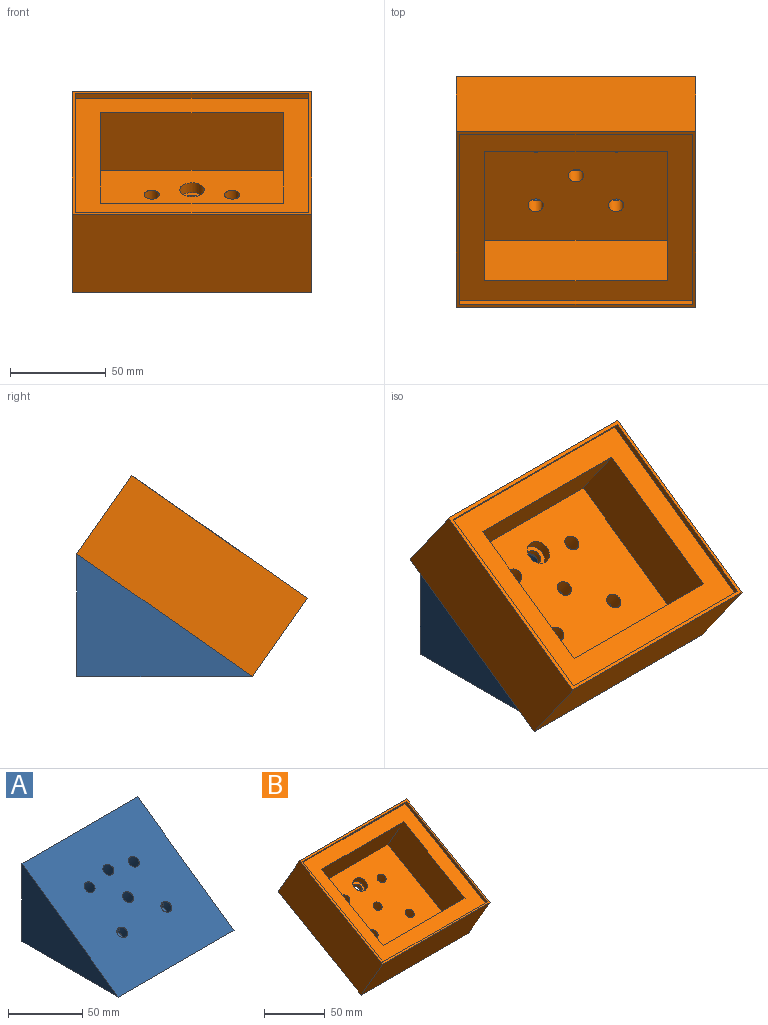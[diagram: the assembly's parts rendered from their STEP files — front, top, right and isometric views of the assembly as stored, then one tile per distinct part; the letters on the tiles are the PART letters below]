
ASSEMBLY  parts=2 mates=1
PART A: 39 faces, bbox 110.1x91.9x64.4 mm
  f0: plane 37.51x3.17mm, normal (0,0,-1), area 116.8mm2, adj f4,f16,f27,f28,f37,f38
  f1: plane 60x36mm, normal (0,0,-1), area 415mm2, adj f11,f16,f17,f18,f27,f28,f30,f31
  f2: cylinder r=4.06mm len=25.14mm, axis (0,-0.57,0.82), area 625mm2, adj f3,f13,f29
  f3: plane 8.13x4.31mm, normal (0,-0.57,0.82), area 35.5mm2, adj f2,f29
  f4: cylinder r=4mm len=16.75mm, axis (0,-0.57,0.82), area 314.3mm2, adj f0,f13,f27,f28,f29
  f5: cylinder r=4mm len=25.07mm, axis (0,-0.57,0.82), area 577.1mm2, adj f6,f13,f29
  f6: plane 5.95x1.09mm, normal (0,-0.57,0.82), area 5.5mm2, adj f5,f29
  f7: cylinder r=4mm len=25.07mm, axis (0,-0.57,0.82), area 577.1mm2, adj f8,f13,f29
  f8: plane 5.95x1.09mm, normal (0,-0.57,0.82), area 5.5mm2, adj f7,f29
  f9: plane 110x64.24mm, normal (0,1,0), area 7040.8mm2, adj f12,f13,f14,f15,f23,f24,f25,f26
  f10: plane 13x6.5mm, normal (0,-1,0), area 58.5mm2, adj f19,f20,f21,f22,f23,f24,f25,f26
  f11: plane 60x18mm, normal (0,-1,0), area 995.5mm2, adj f1,f12,f17,f18,f19,f20,f21,f22
  f12: plane 110x91.75mm, normal (0,0,-1), area 7932.5mm2, adj f9,f11,f13,f14,f15,f16,f17,f18
  f13: plane 110x91.75mm, normal (0,-0.57,0.82), area 12017.4mm2, adj f2,f4,f5,f7,f9,f12,f14,f15
  f14: plane 91.75x64.24mm, normal (1,0,0), area 2947.2mm2, adj f9,f12,f13
  f15: plane 91.75x64.24mm, normal (-1,0,0), area 2947.2mm2, adj f9,f12,f13
  f16: plane 60x18mm, normal (0,1,0), area 1070.3mm2, adj f0,f1,f12,f17,f18,f37,f38
  f17: plane 36x18mm, normal (1,0,0), area 648mm2, adj f1,f11,f12,f16
  f18: plane 36x18mm, normal (-1,0,0), area 648mm2, adj f1,f11,f12,f16
  f19: plane 13x7mm, normal (0,0,-1), area 91mm2, adj f10,f11,f20,f22
  f20: plane 7x6.5mm, normal (1,0,0), area 45.5mm2, adj f10,f11,f19,f21
  f21: plane 13x7mm, normal (0,0,1), area 91mm2, adj f10,f11,f20,f22
  f22: plane 7x6.5mm, normal (-1,0,0), area 45.5mm2, adj f10,f11,f19,f21
  f23: plane 8x0.33mm, normal (0,0,-1), area 2.7mm2, adj f9,f10,f24,f26
  f24: plane 3.25x0.33mm, normal (-1,0,0), area 1.1mm2, adj f9,f10,f23,f25
  f25: plane 8x0.33mm, normal (0,0,1), area 2.7mm2, adj f9,f10,f24,f26
  f26: plane 3.25x0.33mm, normal (1,0,0), area 1.1mm2, adj f9,f10,f23,f25
  f27: plane 23.31x6mm, normal (0,1,0), area 116.8mm2, adj f0,f1,f4,f29,f30,f37
  f28: plane 24.89x6mm, normal (0,1,0), area 126.4mm2, adj f0,f1,f4,f29,f32,f38
  f29: plane 52.59x30.58mm, normal (0,0,-1), area 1437.6mm2, adj f2,f3,f4,f5,f6,f7,f8,f27
  f30: plane 30.45x6mm, normal (1,0,0), area 182.7mm2, adj f1,f27,f29,f31
  f31: plane 52.45x6mm, normal (0,-1,0), area 314.7mm2, adj f1,f29,f30,f32
  f32: plane 30.45x6mm, normal (-1,0,0), area 182.7mm2, adj f1,f28,f29,f31
  f33: cylinder r=4mm len=11.14mm, axis (0,-0.57,0.82), area 176mm2, adj f13,f34,f38
  f34: plane 8x6.35mm, normal (0,-0.57,0.82), area 48.2mm2, adj f33,f38
  f35: cylinder r=4mm len=11.14mm, axis (0,-0.57,0.82), area 176.8mm2, adj f13,f36,f37
  f36: plane 8x6.44mm, normal (0,-0.57,0.82), area 49.4mm2, adj f35,f37
  f37: cylinder r=2.48mm len=16.64mm, axis (0,1,0), area 223mm2, adj f0,f1,f16,f27,f35,f36
  f38: cylinder r=2.55mm len=16.57mm, axis (0,1,0), area 228.2mm2, adj f0,f1,f16,f28,f33,f34
PART B: 24 faces, bbox 125x122x99.3 mm
  f0: plane 125x97mm, normal (0,-0.5,0.87), area 817.2mm2, adj f1,f2,f3,f4,f6,f7,f8,f9
  f1: plane 125x43.3mm, normal (0,-0.87,-0.5), area 6250mm2, adj f0,f2,f4,f5
  f2: plane 122x99.3mm, normal (1,0,0), area 5600mm2, adj f0,f1,f3,f5
  f3: plane 125x43.3mm, normal (0,0.87,0.5), area 6250mm2, adj f0,f2,f4,f5
  f4: plane 122x99.3mm, normal (-1,0,0), area 5600mm2, adj f0,f1,f3,f5
  f5: plane 125x97mm, normal (0,0.5,-0.87), area 13696.8mm2, adj f1,f2,f3,f4,f18,f19,f20,f21
  f6: plane 95.56x57.02mm, normal (1,0,0), area 347.2mm2, adj f0,f7,f9,f10
  f7: plane 121.5x2.77mm, normal (0,0.87,0.5), area 388.8mm2, adj f0,f6,f8,f10
  f8: plane 95.56x57.02mm, normal (-1,0,0), area 347.2mm2, adj f0,f7,f9,f10
  f9: plane 121.5x2.77mm, normal (0,-0.87,-0.5), area 388.8mm2, adj f0,f6,f8,f10
  f10: plane 121.5x93.96mm, normal (0,-0.5,0.87), area 5304mm2, adj f6,f7,f8,f9,f11,f12,f13,f14
  f11: plane 89.85x73.12mm, normal (1,0,0), area 3036mm2, adj f10,f12,f14,f15
  f12: plane 95.5x31.87mm, normal (0,0.87,0.5), area 3514.4mm2, adj f10,f11,f13,f15
  f13: plane 89.85x73.12mm, normal (-1,0,0), area 3036mm2, adj f10,f12,f14,f15
  f14: plane 95.5x31.87mm, normal (0,-0.87,-0.5), area 3514.4mm2, adj f10,f11,f13,f15
  f15: plane 95.5x71.45mm, normal (0,-0.5,0.87), area 7499.7mm2, adj f11,f12,f13,f14,f16,f19,f20,f21
  f16: cylinder r=6.38mm len=14.17mm, axis (0,-0.5,0.87), area 250.3mm2, adj f15,f17
  f17: plane 12.75x11.04mm, normal (0,-0.5,0.87), area 75.8mm2, adj f16,f18
  f18: cylinder r=4.06mm len=8.92mm, axis (0,-0.5,0.87), area 95.8mm2, adj f5,f17
  f19: cylinder r=4mm len=12.66mm, axis (0,-0.5,0.87), area 251.3mm2, adj f5,f15
  f20: cylinder r=4mm len=12.66mm, axis (0,-0.5,0.87), area 251.3mm2, adj f5,f15
  f21: cylinder r=4mm len=12.66mm, axis (0,-0.5,0.87), area 251.3mm2, adj f5,f15
  f22: cylinder r=4mm len=12.66mm, axis (0,-0.5,0.87), area 251.3mm2, adj f5,f15
  f23: cylinder r=4mm len=12.66mm, axis (0,-0.5,0.87), area 251.3mm2, adj f5,f15
PLACE A at identity fixed
PLACE B rot(axis=(1,0,0),5deg) t=(0,-5.31,4.88)mm
MATE fastened A.f13 <-> B.f5  axis (0,-0.57,0.82) through (0,30.64,64.24)mm
